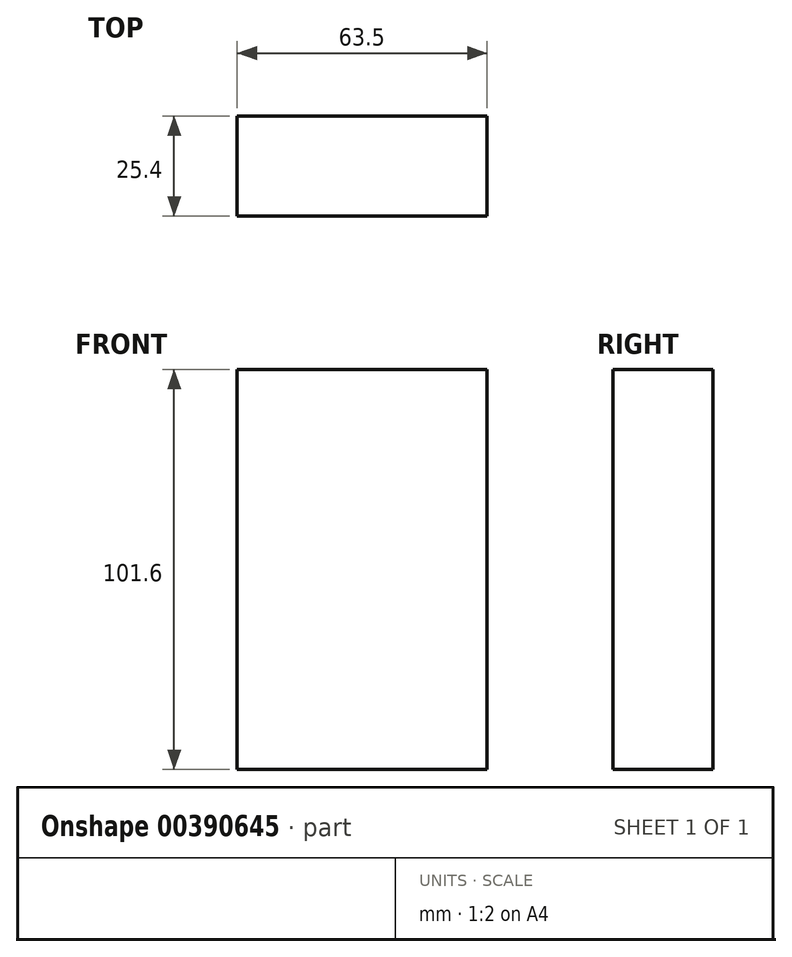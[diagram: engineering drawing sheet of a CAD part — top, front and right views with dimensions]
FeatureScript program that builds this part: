
annotation { "Feature Type Name" : "Feature", "Feature Type Description" : "" }
export const myFeature = defineFeature(function(context is Context, id is Id, definition is map)
    precondition{}
    {
        {
            var Q0;
            Q0=qCreatedBy(makeId("Front.planeOp"),FACE);
            var sketch = newSketch(context, id + "F0", { "sketchPlane" : qUnion([Q0])});
            skLineSegment(sketch, "E0.bottom", {"start": v(-1.94, 46.06) * mm, "end": v(61.56, 46.06) * mm});
            skLineSegment(sketch, "E0.top", {"start": v(-1.94, -55.54) * mm, "end": v(61.56, -55.54) * mm});
            skLineSegment(sketch, "E0.left", {"start": v(-1.94, 46.06) * mm, "end": v(-1.94, -55.54) * mm});
            skLineSegment(sketch, "E0.right", {"start": v(61.56, 46.06) * mm, "end": v(61.56, -55.54) * mm});
            skSolve(sketch);
        }
        {
            var Q0;
            Q0 = qSketchRegion(id + "F0", true);
            var Q1;
            Q1=makeQuery(id+"F0.imprint","IMPRINT",FACE,{"disambiguationData":[TD([[makeQuery(id+"F0.imprint","IMPRINT",EDGE,{"derivedFrom":sQuery(id+"F0.wireOp",EDGE,"E0.bottom")}),-1.0]])]});
            extrude(context, id + "F1", {"entities" : qUnion([Q0, Q1]), "depth" : 25.4 * mm});
        }
    });
